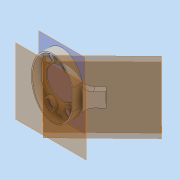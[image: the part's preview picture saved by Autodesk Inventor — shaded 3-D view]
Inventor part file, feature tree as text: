
AUTODESK INVENTOR PART (.ipt)
format: ipt  version: 2019 (Build 230136000, 136)  size: 416,768 bytes
history: native  units: mm
features: other x7, extrude x4, sketch x3, chamfer x1, shell x1
ambient origin geometry x8: Origin, YZ Plane, XZ Plane, XY Plane, X Axis, Y Axis, Z Axis, Center Point
bodies: Body1 (feature_tree), Body2 (feature_tree), Body3 (feature_tree)
feature tree (16):
  other  "Твердое тело1"
  other  "Основной эскиз"
  extrude  "Выдавливание1"  Depth=34.31mm
  sketch  "Эскиз7"
  extrude  "Эллипс"  Depth=8.0mm
  other  "РабПлоскость18"
  sketch  "Эскиз19"
  extrude  "Дырки"  Depth=34.31mm
  chamfer  "Фаска для дырок"  Distance=8.0mm
  shell  "Оболочка12"  Thickness=17.93mm
  other  "РабПлоскость33"
  other  "РабПлоскость34"
  extrude  "Выдавливание23"  Depth=25.93mm
  other  "Твердое тело7"
  sketch  "Эскиз26"
  other  "Твердое тело13"
